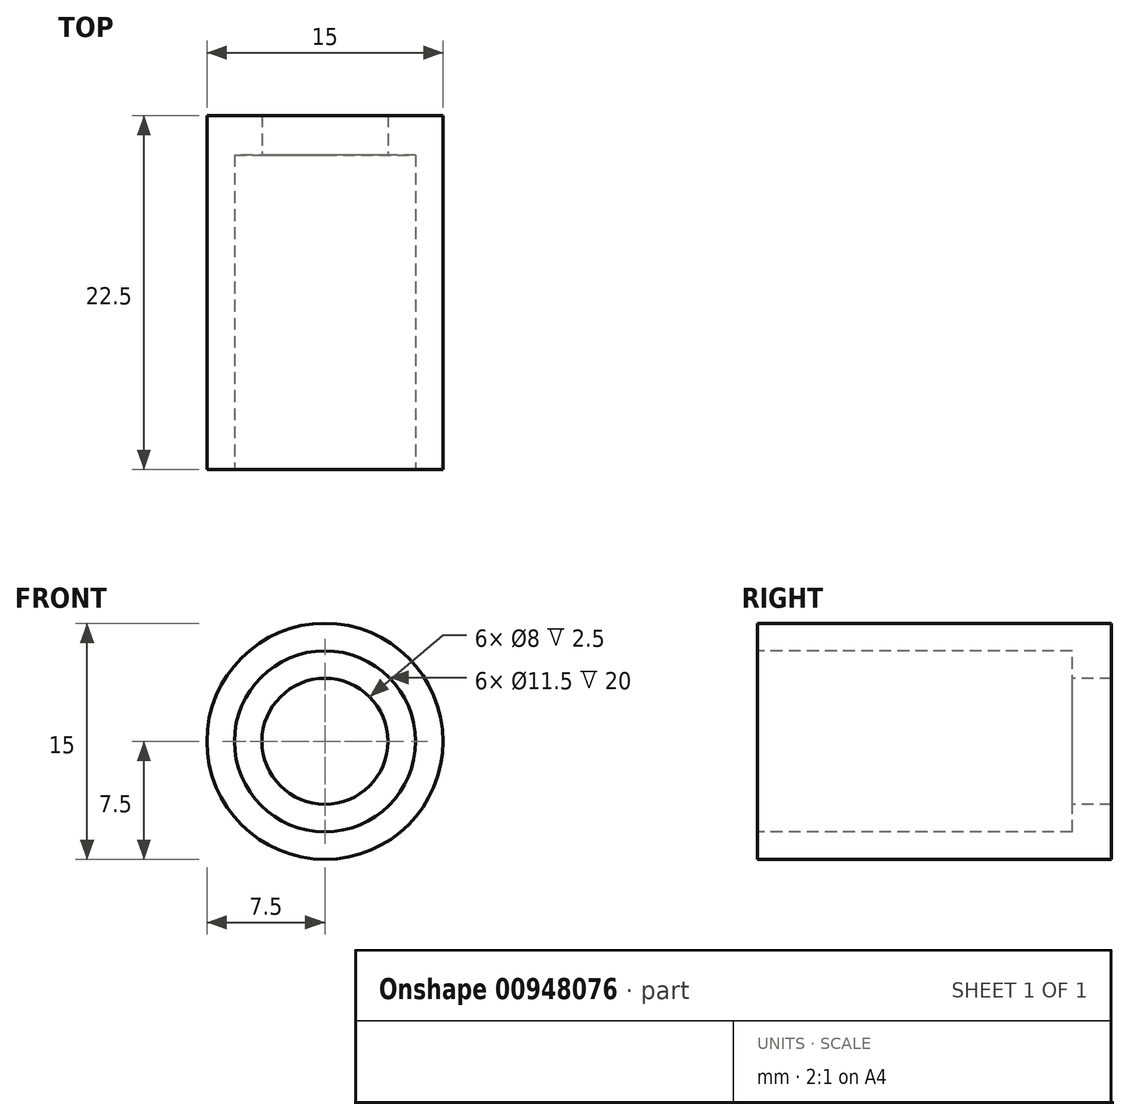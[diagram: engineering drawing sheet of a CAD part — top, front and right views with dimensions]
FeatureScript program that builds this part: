
annotation { "Feature Type Name" : "Feature", "Feature Type Description" : "" }
export const myFeature = defineFeature(function(context is Context, id is Id, definition is map)
    precondition{}
    {
        {
            var Q0;
            Q0=qCreatedBy(makeId("Front.planeOp"),FACE);
            var sketch = newSketch(context, id + "F0", { "sketchPlane" : qUnion([Q0])});
            skCircle(sketch, "E0", {"center": v(0, 0) * mm, "radius": 4 * mm});
            skSolve(sketch);
        }
        {
            var Q0;
            Q0=sQuery(id+"F0.wireOp",EDGE,"E0");
            extrude(context, id + "F1", {"bodyType" : ToolBodyType.SURFACE, "surfaceEntities" : qUnion([Q0]), "depth" : 68 * mm, "offsetDistance" : 25 * mm});
        }
        {
            var Q0;
            Q0=sQuery(id+"F0.wireOp",EDGE,"E0");
            extrude(context, id + "F2", {"bodyType" : ToolBodyType.SURFACE, "surfaceOperationType" : NewSurfaceOperationType.ADD, "surfaceEntities" : qUnion([Q0]), "oppositeDirection" : true, "depth" : 16 * mm, "offsetDistance" : 25 * mm});
        }
        {
            var Q0;
            Q0=qCreatedBy(makeId("Front.planeOp"),FACE);
            var sketch = newSketch(context, id + "F3", { "sketchPlane" : qUnion([Q0])});
            skCircle(sketch, "E1", {"center": v(0, 0) * mm, "radius": 4 * mm});
            skCircle(sketch, "E2", {"center": v(0, 0) * mm, "radius": 7.5 * mm});
            skSolve(sketch);
        }
        {
            var Q0;
            Q0=makeQuery(id+"F3.imprint","IMPRINT",FACE,{"disambiguationData":[TD([[makeQuery(id+"F3.imprint","IMPRINT",EDGE,{"derivedFrom":sQuery(id+"F3.wireOp",EDGE,"E1")}),-1.0]])]});
            extrude(context, id + "F4", {"entities" : qUnion([Q0]), "oppositeDirection" : true, "depth" : 22.5 * mm, "offsetDistance" : 25 * mm});
        }
        {
            var Q0;
            Q0=makeQuery(id+"F4.opExtrude","CAP_FACE",FACE,{"disambiguationData":[OSD([sQuery(id+"F3.wireOp",EDGE,"E1"),sQuery(id+"F3.wireOp",EDGE,"E2")])],"isStart":true});
            var sketch = newSketch(context, id + "F5", { "sketchPlane" : qUnion([Q0])});
            skCircle(sketch, "E3", {"center": v(0, 0) * mm, "radius": 5.75 * mm});
            skCircle(sketch, "E4", {"center": v(0, 0) * mm, "radius": 7.5 * mm});
            skCircle(sketch, "E5", {"center": v(0, 0) * mm, "radius": 4 * mm});
            skSolve(sketch);
        }
        {
            var Q0;
            Q0=makeQuery(id+"F5.imprint","IMPRINT",FACE,{"disambiguationData":[TD([[makeQuery(id+"F5.imprint","IMPRINT",EDGE,{"derivedFrom":sQuery(id+"F5.wireOp",EDGE,"E3")}),1.0]])]});
            extrude(context, id + "F6", {"entities" : qUnion([Q0]), "operationType" : NewBodyOperationType.REMOVE, "oppositeDirection" : true, "depth" : 20 * mm, "offsetDistance" : 25 * mm});
        }
    });
